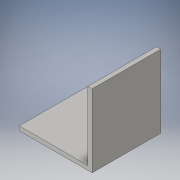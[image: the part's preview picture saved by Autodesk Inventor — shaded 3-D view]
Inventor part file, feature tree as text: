
AUTODESK INVENTOR PART (.ipt)
format: ipt  version: 2016 (Build 200138000, 138)  size: 94,720 bytes
history: native  units: in
note: dims shown in document units (in); Inventor stores cm internally (conversion verified against a paired STEP export)
features: extrude x2, sketch x2
ambient origin geometry x8: Origin, YZ Plane, XZ Plane, XY Plane, X Axis, Y Axis, Z Axis, Center Point
bodies: Solid1 (feature_tree)
feature tree (4):
  extrude  "Extrusion1"  Depth=2.0in
  extrude  "Extrusion2"  Depth=0.125in
  sketch  "Sketch1"  dims[d0=2.125in d1=2.0in]
  sketch  "Sketch2"  dims[d2=0.125in d3=0.0in d4=0.125in d5=2.0in d6=0.0in]
